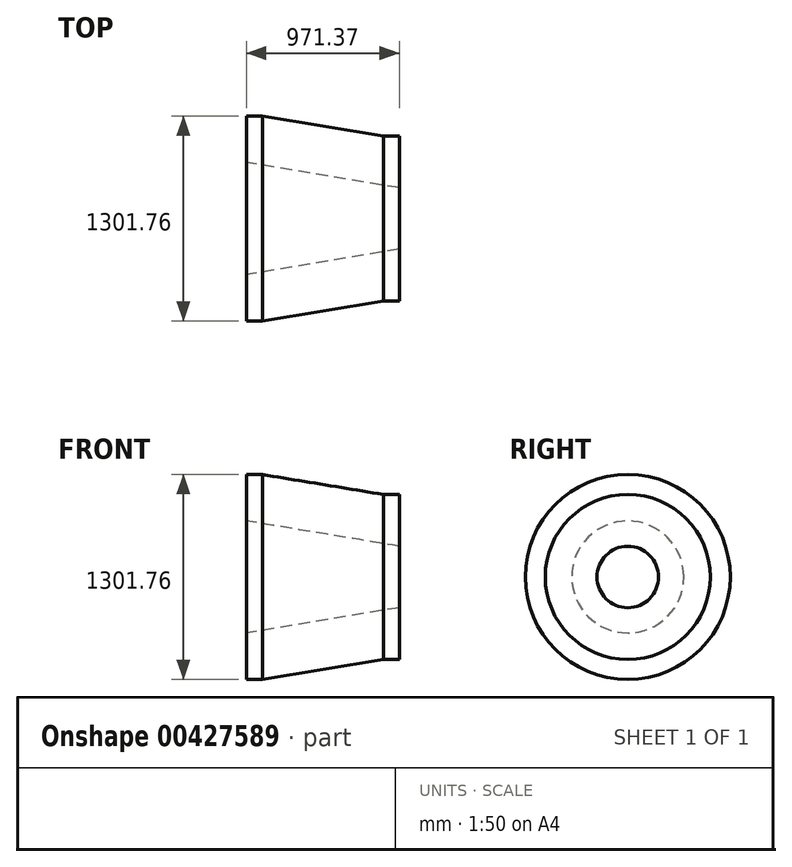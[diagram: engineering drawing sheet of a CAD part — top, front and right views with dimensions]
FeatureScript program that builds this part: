
annotation { "Feature Type Name" : "Feature", "Feature Type Description" : "" }
export const myFeature = defineFeature(function(context is Context, id is Id, definition is map)
    precondition{}
    {
        {
            var Q0;
            Q0=qCreatedBy(makeId("Front.planeOp"),FACE);
            var sketch = newSketch(context, id + "F0", { "sketchPlane" : qUnion([Q0])});
            skLineSegment(sketch, "E0", {"start": v(-568.1, 0) * mm, "end": v(574.9, 0) * mm, "construction": true});
            skLineSegment(sketch, "E1", {"start": v(-471.6, 0) * mm, "end": v(-471.6, 355.6) * mm});
            skLineSegment(sketch, "E2", {"start": v(499.77, 195.26) * mm, "end": v(499.77, 0) * mm});
            skLineSegment(sketch, "E3", {"start": v(-471.6, 355.6) * mm, "end": v(499.77, 195.26) * mm});
            skLineSegment(sketch, "E4", {"start": v(-471.6, 355.6) * mm, "end": v(-471.6, 469.9) * mm});
            skLineSegment(sketch, "E5", {"start": v(-471.6, 650.88) * mm, "end": v(-471.6, 469.9) * mm});
            skLineSegment(sketch, "E6", {"start": v(-471.6, 650.88) * mm, "end": v(-370, 650.88) * mm});
            skLineSegment(sketch, "E7", {"start": v(499.77, 524.08) * mm, "end": v(398.17, 524.08) * mm});
            skLineSegment(sketch, "E8", {"start": v(-370, 650.88) * mm, "end": v(398.17, 524.08) * mm});
            skLineSegment(sketch, "E9", {"start": v(-471.6, 469.9) * mm, "end": v(499.77, 309.56) * mm});
            skLineSegment(sketch, "E10", {"start": v(499.77, 309.56) * mm, "end": v(499.77, 195.26) * mm});
            skLineSegment(sketch, "E11", {"start": v(499.77, 524.08) * mm, "end": v(499.77, 309.56) * mm});
            skSolve(sketch);
        }
        {
            var Q0;
            Q0=makeQuery(id+"F0.imprint","IMPRINT",FACE,{"disambiguationData":[TD([[makeQuery(id+"F0.imprint","IMPRINT",EDGE,{"derivedFrom":sQuery(id+"F0.wireOp",EDGE,"E3")}),1.0]])]});
            var Q1;
            Q1=makeQuery(id+"F0.imprint","IMPRINT",FACE,{"disambiguationData":[TD([[makeQuery(id+"F0.imprint","IMPRINT",EDGE,{"derivedFrom":sQuery(id+"F0.wireOp",EDGE,"E5")}),1.0]])]});
            var Q2;
            Q2=sQuery(id+"F0.wireOp",EDGE,"E0");
            revolve(context, id + "F1", {"surfaceOperationType" : NewSurfaceOperationType.NEW, "entities" : qUnion([Q0, Q1]), "axis" : qUnion([Q2]), "revolveType" : RevolveType.FULL});
        }
    });
